# Revit family: Legrand Caja Plexo³ 18 módulos
name_source: partatom
category: Equipement électrique
revit_build: Autodesk Revit 2018 (Build: 20170223_1515(x64)
units: mm (PartAtom-declared; Revit-internal decimal feet)

## family parameters
Basée sur le plan de construction = Non
Configuration du panneau = Deux colonnes, circuits au sein
Cote de connecteur circulaire = Utiliser le diamètre
Couper avec des vides une fois chargée = Non
Numéro OmniClass = 23.80.30.11.17
Partagée = Non
Point de calcul de pièce = Non
Titre OmniClass = Distribution Boards and Control Panels
Toujours verticalement = Oui
Type d'élément = Tableau de raccordement

## types (18) — shared parameters
Caja 601835 = Non
Condiciones Generales de Uso = https://export.legrand.com
ETIM Class 6.0 = EC000214
Fabricant = Legrand
IK = 09
IP = 65
Image du type = plexo3_18_rangees_001926_pw_174335_pz_0.jpg
Materia = Poliestireno
RAL = 7046
URL = www.legrand.fr

## per-type parameters (varying)
| type | Bornas N | Bornas T | Caja 001924 | Caja 001925 | Caja 001926 | Caja 001927 | Caja 601836 | Caja 601837 | Caja 601838 | Caja 601946 | Caja 601947 | Caja 601948 | Caja 601965 | Caja 601966 | Caja 601967 | Caja 601968 | Caja 601985 | Caja 601986 | Caja 601987 | Caja 601988 |
| Plexo³ 18 módulos de 1 fila 001924 |  | terminal 5+18 hoyos | Oui | Non | Non | Non | Non | Non | Non | Non | Non | Non | Non | Non | Non | Non | Non | Non | Non | Non |
| Plexo³ 18 módulos de 2 filas 001925 |  | terminal 5+27 hoyos | Non | Oui | Non | Non | Non | Non | Non | Non | Non | Non | Non | Non | Non | Non | Non | Non | Non | Non |
| Plexo³ 18 módulos de 3 filas 001926 |  | terminal 5+36 hoyos | Non | Non | Oui | Non | Non | Non | Non | Non | Non | Non | Non | Non | Non | Non | Non | Non | Non | Non |
| Plexo³ 18 módulos de 4 filas 001927 |  | terminal 5+45 hoyos | Non | Non | Non | Oui | Non | Non | Non | Non | Non | Non | Non | Non | Non | Non | Non | Non | Non | Non |
| Plexo³ 18 módulos de 1 fila 601965 |  | terminal 17 hoyos | Non | Non | Non | Non | Non | Non | Non | Non | Non | Non | Oui | Non | Non | Non | Non | Non | Non | Non |
| Plexo³ 18 módulos de 1 fila 601985 | terminal 17 hoyos | terminal 17 hoyos | Non | Non | Non | Non | Non | Non | Non | Non | Non | Non | Non | Non | Non | Non | Oui | Non | Non | Non |
| Plexo³ 18 módulos de 2 filas 601836 |  |  | Non | Non | Non | Non | Oui | Non | Non | Non | Non | Non | Non | Non | Non | Non | Non | Non | Non | Non |
| Plexo³ 18 módulos de 2 filas 601946 |  |  | Non | Non | Non | Non | Non | Non | Non | Oui | Non | Non | Non | Non | Non | Non | Non | Non | Non | Non |
| Plexo³ 18 módulos de 2 filas 601966 |  | terminal 22 hoyos | Non | Non | Non | Non | Non | Non | Non | Non | Non | Non | Non | Oui | Non | Non | Non | Non | Non | Non |
| Plexo³ 18 módulos de 2 filas 601986 | terminal 22 hoyos | terminal 22 hoyos | Non | Non | Non | Non | Non | Non | Non | Non | Non | Non | Non | Non | Non | Non | Non | Oui | Non | Non |
| Plexo³ 18 módulos de 3 filas 601947 |  |  | Non | Non | Non | Non | Non | Non | Non | Non | Oui | Non | Non | Non | Non | Non | Non | Non | Non | Non |
| Plexo³ 18 módulos de 3 filas 601967 |  | IDS_27_TROUS | Non | Non | Non | Non | Non | Non | Non | Non | Non | Non | Non | Non | Oui | Non | Non | Non | Non | Non |
| Plexo³ 18 módulos de 3 filas 601987 | IDS_27_TROUS | IDS_27_TROUS | Non | Non | Non | Non | Non | Non | Non | Non | Non | Non | Non | Non | Non | Non | Non | Non | Oui | Non |
| Plexo³ 18 módulos de 4 filas 601838 |  |  | Non | Non | Non | Non | Non | Non | Oui | Non | Non | Non | Non | Non | Non | Non | Non | Non | Non | Non |
| Plexo³ 18 módulos de 4 filas 601948 |  |  | Non | Non | Non | Non | Non | Non | Non | Non | Non | Oui | Non | Non | Non | Non | Non | Non | Non | Non |
| Plexo³ 18 módulos de 4 filas 601968 |  | terminal 35 hoyos | Non | Non | Non | Non | Non | Non | Non | Non | Non | Non | Non | Non | Non | Oui | Non | Non | Non | Non |
| Plexo³ 18 módulos de 4 filas 601988 | terminal 35 hoyos | terminal 35 hoyos | Non | Non | Non | Non | Non | Non | Non | Non | Non | Non | Non | Non | Non | Non | Non | Non | Non | Oui |
| Plexo³ 18 módulos de 3 filas 601837 |  |  | Non | Non | Non | Non | Non | Oui | Non | Non | Non | Non | Non | Non | Non | Non | Non | Non | Non | Non |

note: column(s) folded — value = type name in every type: Description
